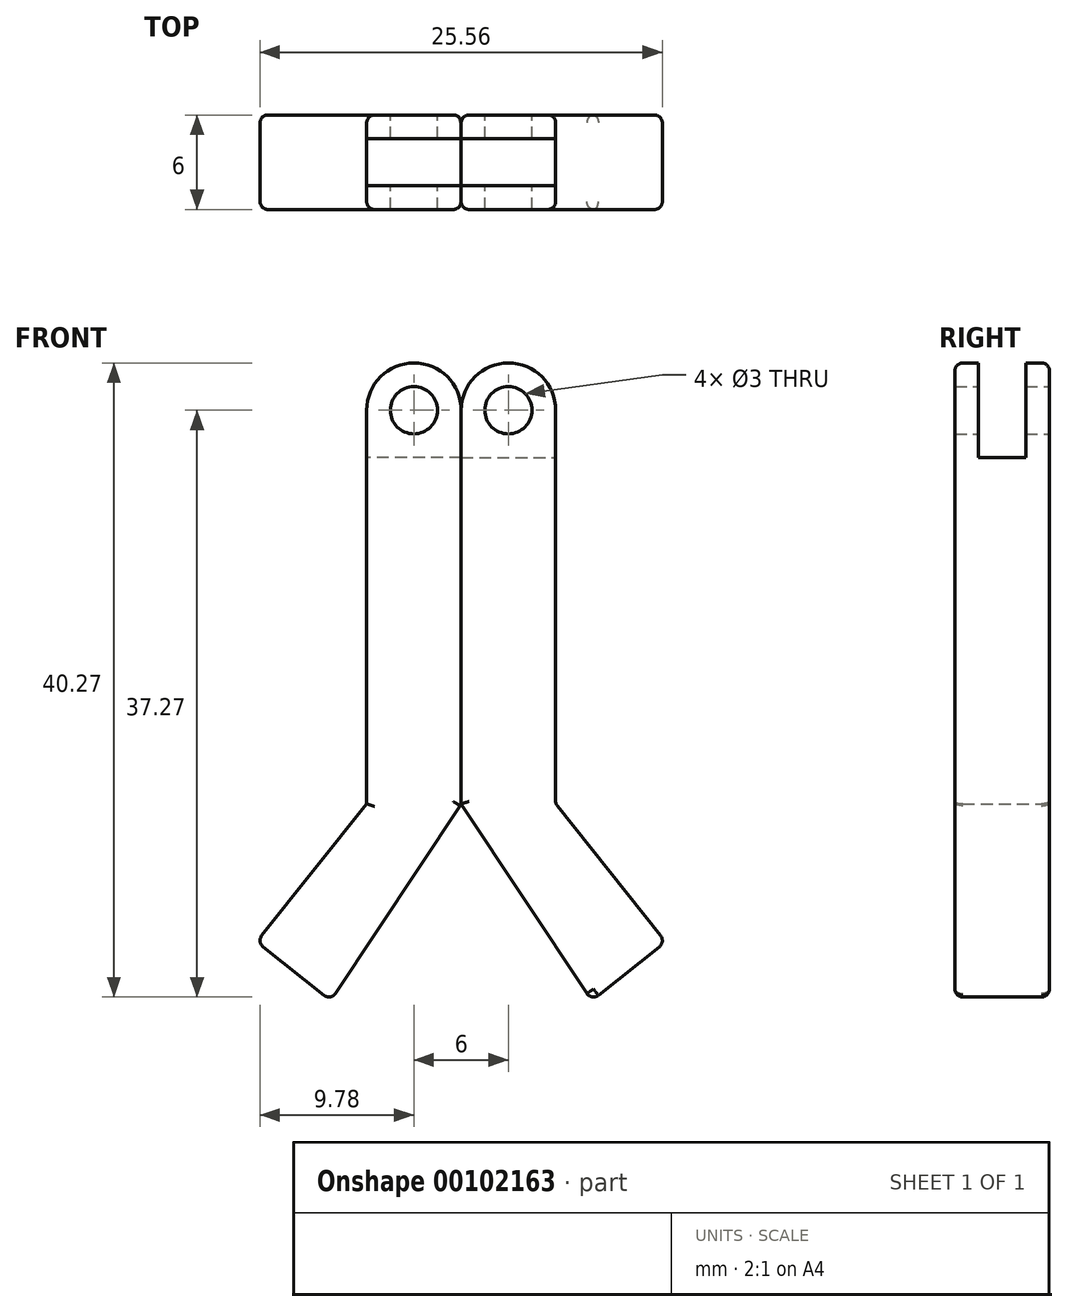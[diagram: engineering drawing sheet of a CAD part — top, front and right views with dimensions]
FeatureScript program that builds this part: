
annotation { "Feature Type Name" : "Feature", "Feature Type Description" : "" }
export const myFeature = defineFeature(function(context is Context, id is Id, definition is map)
    precondition{}
    {
        {
            var Q0;
            Q0=qCreatedBy(makeId("Front.planeOp"),FACE);
            var sketch = newSketch(context, id + "F0", { "sketchPlane" : qUnion([Q0])});
            skLineSegment(sketch, "E0", {"start": v(0, 0) * mm, "end": v(0, 25) * mm});
            skArc(sketch, "E1", {"start": v(0, 25) * mm, "mid": v(-3, 28) * mm, "end": v(-6, 25) * mm});
            skLineSegment(sketch, "E2", {"start": v(-6, 25) * mm, "end": v(-6, 0) * mm});
            skLineSegment(sketch, "E3", {"start": v(-6, 0) * mm, "end": v(-12.98, -8.77) * mm});
            skLineSegment(sketch, "E4", {"start": v(-12.98, -8.77) * mm, "end": v(-8.29, -12.5) * mm});
            skLineSegment(sketch, "E5", {"start": v(-8.29, -12.5) * mm, "end": v(0, 0) * mm});
            skCircle(sketch, "E6", {"center": v(-3, 25) * mm, "radius": 1.5 * mm});
            skSolve(sketch);
        }
        {
            var Q0;
            Q0=makeQuery(id+"F0.imprint","IMPRINT",FACE,{"disambiguationData":[TD([[makeQuery(id+"F0.imprint","IMPRINT",EDGE,{"derivedFrom":sQuery(id+"F0.wireOp",EDGE,"E0")}),1.0]])]});
            extrude(context, id + "F1", {"entities" : qUnion([Q0]), "depth" : 6 * mm, "symmetric" : true});
        }
        {
            var Q0;
            Q0=makeQuery(id+"F1.opExtrude","SWEPT_FACE",FACE,{"disambiguationData":[OSD([sQuery(id+"F0.wireOp",EDGE,"E2")])]});
            var sketch = newSketch(context, id + "F2", { "sketchPlane" : qUnion([Q0])});
            skLineSegment(sketch, "E7", {"start": v(0, 25) * mm, "end": v(0, 22) * mm, "construction": true});
            skPoint(sketch, "E7.endSnap0", {"position": v(0, 25) * mm});
            skLineSegment(sketch, "E8", {"start": v(-7.52, 22) * mm, "end": v(15.83, 22) * mm, "construction": true});
            skLineSegment(sketch, "E9.bottom", {"start": v(-1.5, 22) * mm, "end": v(1.5, 22) * mm});
            skLineSegment(sketch, "E9.top", {"start": v(-1.5, 30.42) * mm, "end": v(1.5, 30.42) * mm});
            skLineSegment(sketch, "E9.left", {"start": v(-1.5, 22) * mm, "end": v(-1.5, 30.42) * mm});
            skLineSegment(sketch, "E9.right", {"start": v(1.5, 22) * mm, "end": v(1.5, 30.42) * mm});
            skLineSegment(sketch, "E10", {"start": v(0, 34.21) * mm, "end": v(0, 16.29) * mm, "construction": true});
            skSolve(sketch);
        }
        {
            var Q0;
            {var subQ0=sQuery(id+"F2.wireOp",EDGE,"E9.top");Q0=makeQuery(id+"F2.imprint","IMPRINT",FACE,{"disambiguationData":[TD([[makeQuery(id+"F2.imprint","IMPRINT",EDGE,{"derivedFrom":subQ0}),-1.0]])]});}
            var Q1;
            {var subQ0=sQuery(id+"F2.wireOp",EDGE,"E9.bottom");Q1=makeQuery(id+"F2.imprint","IMPRINT",FACE,{"disambiguationData":[TD([[makeQuery(id+"F2.imprint","IMPRINT",EDGE,{"derivedFrom":subQ0}),1.0]])]});}
            extrude(context, id + "F3", {"entities" : qUnion([Q0, Q1]), "operationType" : NewBodyOperationType.REMOVE, "endBound" : BoundingType.THROUGH_ALL, "oppositeDirection" : true, "depth" : 25 * mm});
        }
        {
            var Q0;
            Q0=makeQuery(id+"F1.opExtrude","SWEPT_BODY",BODY,{"disambiguationData":[OSD([sQuery(id+"F0.wireOp",EDGE,"E0"),sQuery(id+"F0.wireOp",EDGE,"E1"),sQuery(id+"F0.wireOp",EDGE,"E2"),sQuery(id+"F0.wireOp",EDGE,"E3"),sQuery(id+"F0.wireOp",EDGE,"E4"),sQuery(id+"F0.wireOp",EDGE,"E5"),sQuery(id+"F0.wireOp",EDGE,"E6")])]});
            var Q1;
            Q1=qCreatedBy(makeId("Right.planeOp"),FACE);
            mirror(context, id + "F4", {"entities" : qUnion([Q0]), "mirrorPlane" : qUnion([Q1])});
        }
        {
            var Q0;
            Q0=makeQuery(id+"F4.opPattern","COPY",EDGE,{"derivedFrom":makeQuery(id+"F1.opExtrude","CAP_EDGE",EDGE,{"disambiguationData":[OSD([sQuery(id+"F0.wireOp",EDGE,"E2")])],"isStart":false}),"instanceName":"1"});
            var Q1;
            Q1=makeQuery(id+"F1.opExtrude","CAP_EDGE",EDGE,{"disambiguationData":[OSD([sQuery(id+"F0.wireOp",EDGE,"E2")])],"isStart":false});
            var Q2;
            Q2=makeQuery(id+"F1.opExtrude","CAP_EDGE",EDGE,{"disambiguationData":[OSD([sQuery(id+"F0.wireOp",EDGE,"E5")])],"isStart":false});
            var Q3;
            Q3=makeQuery(id+"F1.opExtrude","CAP_EDGE",EDGE,{"disambiguationData":[OSD([sQuery(id+"F0.wireOp",EDGE,"E3")])],"isStart":false});
            var Q4;
            Q4=makeQuery(id+"F1.opExtrude","CAP_EDGE",EDGE,{"disambiguationData":[OSD([sQuery(id+"F0.wireOp",EDGE,"E4")])],"isStart":false});
            var Q5;
            Q5=makeQuery(id+"F4.opPattern","COPY",EDGE,{"derivedFrom":makeQuery(id+"F1.opExtrude","CAP_EDGE",EDGE,{"disambiguationData":[OSD([sQuery(id+"F0.wireOp",EDGE,"E5")])],"isStart":false}),"instanceName":"1"});
            var Q6;
            Q6=makeQuery(id+"F4.opPattern","COPY",EDGE,{"derivedFrom":makeQuery(id+"F1.opExtrude","CAP_EDGE",EDGE,{"disambiguationData":[OSD([sQuery(id+"F0.wireOp",EDGE,"E3")])],"isStart":false}),"instanceName":"1"});
            var Q7;
            Q7=makeQuery(id+"F4.opPattern","COPY",EDGE,{"derivedFrom":makeQuery(id+"F1.opExtrude","CAP_EDGE",EDGE,{"disambiguationData":[OSD([sQuery(id+"F0.wireOp",EDGE,"E3")])],"isStart":true}),"instanceName":"1"});
            var Q8;
            Q8=makeQuery(id+"F4.opPattern","COPY",EDGE,{"derivedFrom":makeQuery(id+"F1.opExtrude","SWEPT_EDGE",EDGE,{"disambiguationData":[OSD([sQuery(id+"F0.wireOp",EDGE,"E2"),sQuery(id+"F0.wireOp",EDGE,"E3")])]}),"instanceName":"1"});
            var Q9;
            Q9=makeQuery(id+"F4.opPattern","COPY",EDGE,{"derivedFrom":makeQuery(id+"F1.opExtrude","CAP_EDGE",EDGE,{"disambiguationData":[OSD([sQuery(id+"F0.wireOp",EDGE,"E2")])],"isStart":true}),"instanceName":"1"});
            var Q10;
            Q10=makeQuery(id+"F1.opExtrude","CAP_EDGE",EDGE,{"disambiguationData":[OSD([sQuery(id+"F0.wireOp",EDGE,"E0")])],"isStart":true});
            var Q11;
            Q11=makeQuery(id+"F1.opExtrude","CAP_EDGE",EDGE,{"disambiguationData":[OSD([sQuery(id+"F0.wireOp",EDGE,"E2")])],"isStart":true});
            var Q12;
            Q12=makeQuery(id+"F1.opExtrude","CAP_EDGE",EDGE,{"disambiguationData":[OSD([sQuery(id+"F0.wireOp",EDGE,"E3")])],"isStart":true});
            var Q13;
            Q13=makeQuery(id+"F1.opExtrude","CAP_EDGE",EDGE,{"disambiguationData":[OSD([sQuery(id+"F0.wireOp",EDGE,"E5")])],"isStart":true});
            var Q14;
            Q14=makeQuery(id+"F1.opExtrude","CAP_EDGE",EDGE,{"disambiguationData":[OSD([sQuery(id+"F0.wireOp",EDGE,"E4")])],"isStart":true});
            var Q15;
            Q15=makeQuery(id+"F1.opExtrude","SWEPT_EDGE",EDGE,{"disambiguationData":[OSD([sQuery(id+"F0.wireOp",EDGE,"E4"),sQuery(id+"F0.wireOp",EDGE,"E5")])]});
            var Q16;
            Q16=makeQuery(id+"F4.opPattern","COPY",EDGE,{"derivedFrom":makeQuery(id+"F1.opExtrude","CAP_EDGE",EDGE,{"disambiguationData":[OSD([sQuery(id+"F0.wireOp",EDGE,"E5")])],"isStart":true}),"instanceName":"1"});
            var Q17;
            Q17=makeQuery(id+"F4.opPattern","COPY",EDGE,{"derivedFrom":makeQuery(id+"F1.opExtrude","CAP_EDGE",EDGE,{"disambiguationData":[OSD([sQuery(id+"F0.wireOp",EDGE,"E4")])],"isStart":true}),"instanceName":"1"});
            var Q18;
            Q18=makeQuery(id+"F4.opPattern","COPY",FACE,{"derivedFrom":makeQuery(id+"F1.opExtrude","SWEPT_FACE",FACE,{"disambiguationData":[OSD([sQuery(id+"F0.wireOp",EDGE,"E3")])]}),"instanceName":"1"});
            var Q19;
            Q19=makeQuery(id+"F4.opPattern","COPY",EDGE,{"derivedFrom":makeQuery(id+"F1.opExtrude","CAP_EDGE",EDGE,{"disambiguationData":[OSD([sQuery(id+"F0.wireOp",EDGE,"E4")])],"isStart":false}),"instanceName":"1"});
            var Q20;
            Q20=makeQuery(id+"F1.opExtrude","SWEPT_EDGE",EDGE,{"disambiguationData":[OSD([sQuery(id+"F0.wireOp",EDGE,"E3"),sQuery(id+"F0.wireOp",EDGE,"E4")])]});
            fillet(context, id + "F5", {"entities" : qUnion([Q0, Q1, Q2, Q3, Q4, Q5, Q6, Q7, Q8, Q9, Q10, Q11, Q12, Q13, Q14, Q15, Q16, Q17, Q18, Q19, Q20]), "radius" : .5 * mm, "tangentPropagation" : true, "allowEdgeOverflow" : false});
        }
        {
            var Q0;
            Q0=makeQuery(id+"F4.opPattern","COPY",EDGE,{"derivedFrom":makeQuery(id+"F1.opExtrude","SWEPT_EDGE",EDGE,{"disambiguationData":[OSD([sQuery(id+"F0.wireOp",EDGE,"E4"),sQuery(id+"F0.wireOp",EDGE,"E5")])]}),"instanceName":"1"});
            fillet(context, id + "F6", {"entities" : qUnion([Q0]), "radius" : .5 * mm, "tangentPropagation" : true, "allowEdgeOverflow" : false});
        }
        {
            var Q0;
            Q0=makeQuery(id+"F1.opExtrude","SWEPT_EDGE",EDGE,{"disambiguationData":[OSD([sQuery(id+"F0.wireOp",EDGE,"E0"),sQuery(id+"F0.wireOp",EDGE,"E5")])]});
            fillet(context, id + "F7", {"entities" : qUnion([Q0]), "radius" : .5 * mm, "tangentPropagation" : true, "allowEdgeOverflow" : false});
        }
    });
